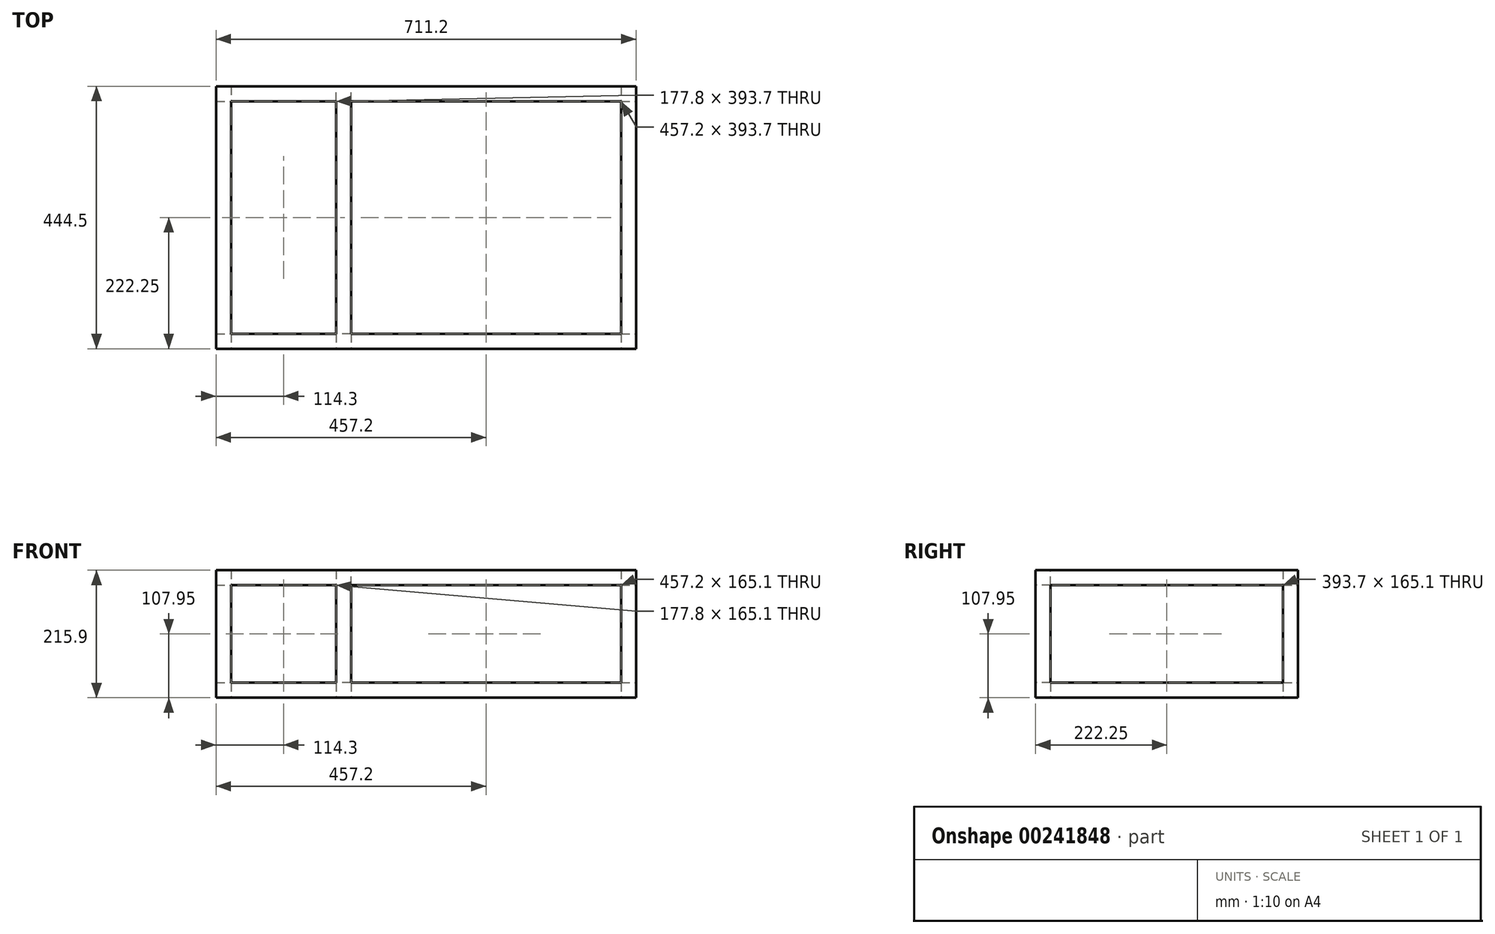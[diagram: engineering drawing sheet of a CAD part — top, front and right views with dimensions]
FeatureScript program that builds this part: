
annotation { "Feature Type Name" : "Feature", "Feature Type Description" : "" }
export const myFeature = defineFeature(function(context is Context, id is Id, definition is map)
    precondition{}
    {
        {
            var Q0;
            Q0=qCreatedBy(makeId("Top.planeOp"),FACE);
            var sketch = newSketch(context, id + "F0", { "sketchPlane" : qUnion([Q0])});
            skLineSegment(sketch, "E0.bottom", {"start": v(0, 0) * mm, "end": v(711.2, 0) * mm});
            skLineSegment(sketch, "E0.top", {"start": v(0, 444.5) * mm, "end": v(711.2, 444.5) * mm});
            skLineSegment(sketch, "E0.left", {"start": v(0, 0) * mm, "end": v(0, 444.5) * mm});
            skLineSegment(sketch, "E0.right", {"start": v(711.2, 0) * mm, "end": v(711.2, 444.5) * mm});
            skLineSegment(sketch, "E1.bottom", {"start": v(25.4, 25.4) * mm, "end": v(685.8, 25.4) * mm});
            skLineSegment(sketch, "E1.top", {"start": v(25.4, 419.1) * mm, "end": v(685.8, 419.1) * mm});
            skLineSegment(sketch, "E1.left", {"start": v(25.4, 25.4) * mm, "end": v(25.4, 419.1) * mm});
            skLineSegment(sketch, "E1.right", {"start": v(685.8, 25.4) * mm, "end": v(685.8, 419.1) * mm});
            skSolve(sketch);
        }
        {
            var Q0;
            Q0 = qSketchRegion(id + "F0", true);
            extrude(context, id + "F1", {"entities" : qUnion([Q0]), "depth" : 215.9 * mm});
        }
        {
            var Q0;
            Q0=makeQuery(id+"F1.opExtrude","SWEPT_FACE",FACE,{"disambiguationData":[OSD([sQuery(id+"F0.wireOp",EDGE,"E0.bottom")])]});
            var sketch = newSketch(context, id + "F2", { "sketchPlane" : qUnion([Q0])});
            skLineSegment(sketch, "E2.bottom", {"start": v(25.4, 190.5) * mm, "end": v(685.8, 190.5) * mm});
            skLineSegment(sketch, "E2.top", {"start": v(25.4, 25.4) * mm, "end": v(685.8, 25.4) * mm});
            skLineSegment(sketch, "E2.left", {"start": v(25.4, 190.5) * mm, "end": v(25.4, 25.4) * mm});
            skLineSegment(sketch, "E2.right", {"start": v(685.8, 190.5) * mm, "end": v(685.8, 25.4) * mm});
            skSolve(sketch);
        }
        {
            var Q0;
            Q0 = qSketchRegion(id + "F2", true);
            extrude(context, id + "F3", {"entities" : qUnion([Q0]), "operationType" : NewBodyOperationType.REMOVE, "endBound" : BoundingType.THROUGH_ALL, "oppositeDirection" : true, "depth" : 25.4 * mm});
        }
        {
            var Q0;
            Q0=makeQuery(id+"F1.opExtrude","SWEPT_FACE",FACE,{"disambiguationData":[OSD([sQuery(id+"F0.wireOp",EDGE,"E0.right")])]});
            var sketch = newSketch(context, id + "F4", { "sketchPlane" : qUnion([Q0])});
            skLineSegment(sketch, "E3.bottom", {"start": v(25.4, 190.5) * mm, "end": v(419.1, 190.5) * mm});
            skLineSegment(sketch, "E3.top", {"start": v(25.4, 25.4) * mm, "end": v(419.1, 25.4) * mm});
            skLineSegment(sketch, "E3.left", {"start": v(25.4, 190.5) * mm, "end": v(25.4, 25.4) * mm});
            skLineSegment(sketch, "E3.right", {"start": v(419.1, 190.5) * mm, "end": v(419.1, 25.4) * mm});
            skSolve(sketch);
        }
        {
            var Q0;
            Q0 = qSketchRegion(id + "F4", true);
            extrude(context, id + "F5", {"entities" : qUnion([Q0]), "operationType" : NewBodyOperationType.REMOVE, "endBound" : BoundingType.THROUGH_ALL, "oppositeDirection" : true, "depth" : 25.4 * mm});
        }
        {
            var Q0;
            {var subQ2=sQuery(id+"F0.wireOp",EDGE,"E1.top");Q0=makeQuery(id+"F3.boolean.opBoolean","SPLIT",FACE,{"disambiguationData":[TD([makeQuery(id+"F3.opExtrude","SWEPT_FACE",FACE,{"disambiguationData":[OSD([sQuery(id+"F2.wireOp",EDGE,"E2.bottom")])]})])],"derivedFrom":makeQuery(id+"F1.opExtrude","SWEPT_FACE",FACE,{"disambiguationData":[OSD([subQ2])]})});}
            var sketch = newSketch(context, id + "F6", { "sketchPlane" : qUnion([Q0])});
            skLineSegment(sketch, "E4.bottom", {"start": v(228.6, 215.9) * mm, "end": v(203.2, 215.9) * mm});
            skLineSegment(sketch, "E4.top", {"start": v(228.6, 190.5) * mm, "end": v(203.2, 190.5) * mm});
            skLineSegment(sketch, "E4.left", {"start": v(228.6, 215.9) * mm, "end": v(228.6, 190.5) * mm});
            skLineSegment(sketch, "E4.right", {"start": v(203.2, 215.9) * mm, "end": v(203.2, 190.5) * mm});
            skSolve(sketch);
        }
        {
            var Q0;
            Q0=makeQuery(id+"F6.imprint","IMPRINT",FACE,{"disambiguationData":[TD([[makeQuery(id+"F6.imprint","IMPRINT",EDGE,{"derivedFrom":sQuery(id+"F6.wireOp",EDGE,"E4.bottom")}),-1.0]])]});
            extrude(context, id + "F7", {"entities" : qUnion([Q0]), "operationType" : NewBodyOperationType.ADD, "endBound" : BoundingType.UP_TO_NEXT, "depth" : 25.4 * mm});
        }
        {
            var Q0;
            {var subQ2=sQuery(id+"F0.wireOp",EDGE,"E1.bottom");Q0=makeQuery(id+"F3.boolean.opBoolean","SPLIT",FACE,{"disambiguationData":[TD([makeQuery(id+"F3.opExtrude","SWEPT_FACE",FACE,{"disambiguationData":[OSD([sQuery(id+"F2.wireOp",EDGE,"E2.top")])]})])],"derivedFrom":makeQuery(id+"F1.opExtrude","SWEPT_FACE",FACE,{"disambiguationData":[OSD([subQ2])]})});}
            var sketch = newSketch(context, id + "F8", { "sketchPlane" : qUnion([Q0])});
            skLineSegment(sketch, "E5.bottom", {"start": v(-228.6, 25.4) * mm, "end": v(-203.2, 25.4) * mm});
            skLineSegment(sketch, "E5.top", {"start": v(-228.6, 0) * mm, "end": v(-203.2, 0) * mm});
            skLineSegment(sketch, "E5.left", {"start": v(-228.6, 25.4) * mm, "end": v(-228.6, 0) * mm});
            skLineSegment(sketch, "E5.right", {"start": v(-203.2, 25.4) * mm, "end": v(-203.2, 0) * mm});
            skSolve(sketch);
        }
        {
            var Q0;
            Q0 = qSketchRegion(id + "F8", true);
            extrude(context, id + "F9", {"entities" : qUnion([Q0]), "operationType" : NewBodyOperationType.ADD, "endBound" : BoundingType.UP_TO_NEXT, "depth" : 25.4 * mm});
        }
        {
            var Q0;
            {var subQ4=makeQuery(id+"F3.opExtrude","SWEPT_FACE",FACE,{"disambiguationData":[OSD([sQuery(id+"F2.wireOp",EDGE,"E2.bottom")])]});Q0=makeQuery(id+"F7.boolean.opBoolean","MERGE",FACE,{"derivedFrom":[makeQuery(id+"F3.boolean.opBoolean","COPY",FACE,{"disambiguationData":[TD([makeQuery(id+"F1.opExtrude","SWEPT_FACE",FACE,{"disambiguationData":[OSD([sQuery(id+"F0.wireOp",EDGE,"E0.bottom")])]})])],"derivedFrom":subQ4}),makeQuery(id+"F3.boolean.opBoolean","COPY",FACE,{"disambiguationData":[TD([makeQuery(id+"F1.opExtrude","SWEPT_FACE",FACE,{"disambiguationData":[OSD([sQuery(id+"F0.wireOp",EDGE,"E0.top")])]})])],"derivedFrom":subQ4}),makeQuery(id+"F7.opExtrude","SWEPT_FACE",FACE,{"disambiguationData":[OSD([sQuery(id+"F6.wireOp",EDGE,"E4.top")])]})]});}
            var sketch = newSketch(context, id + "F10", { "sketchPlane" : qUnion([Q0])});
            skLineSegment(sketch, "E6.bottom", {"start": v(228.6, -419.1) * mm, "end": v(203.2, -419.1) * mm});
            skLineSegment(sketch, "E6.top", {"start": v(228.6, -444.5) * mm, "end": v(203.2, -444.5) * mm});
            skLineSegment(sketch, "E6.left", {"start": v(228.6, -419.1) * mm, "end": v(228.6, -444.5) * mm});
            skLineSegment(sketch, "E6.right", {"start": v(203.2, -419.1) * mm, "end": v(203.2, -444.5) * mm});
            skLineSegment(sketch, "E7.bottom", {"start": v(228.6, -25.4) * mm, "end": v(203.2, -25.4) * mm});
            skLineSegment(sketch, "E7.top", {"start": v(228.6, 0) * mm, "end": v(203.2, 0) * mm});
            skLineSegment(sketch, "E7.left", {"start": v(228.6, -25.4) * mm, "end": v(228.6, 0) * mm});
            skLineSegment(sketch, "E7.right", {"start": v(203.2, -25.4) * mm, "end": v(203.2, 0) * mm});
            skSolve(sketch);
        }
        {
            var Q0;
            Q0 = qSketchRegion(id + "F10", true);
            extrude(context, id + "F11", {"entities" : qUnion([Q0]), "operationType" : NewBodyOperationType.ADD, "endBound" : BoundingType.UP_TO_NEXT, "depth" : 25.4 * mm});
        }
    });
